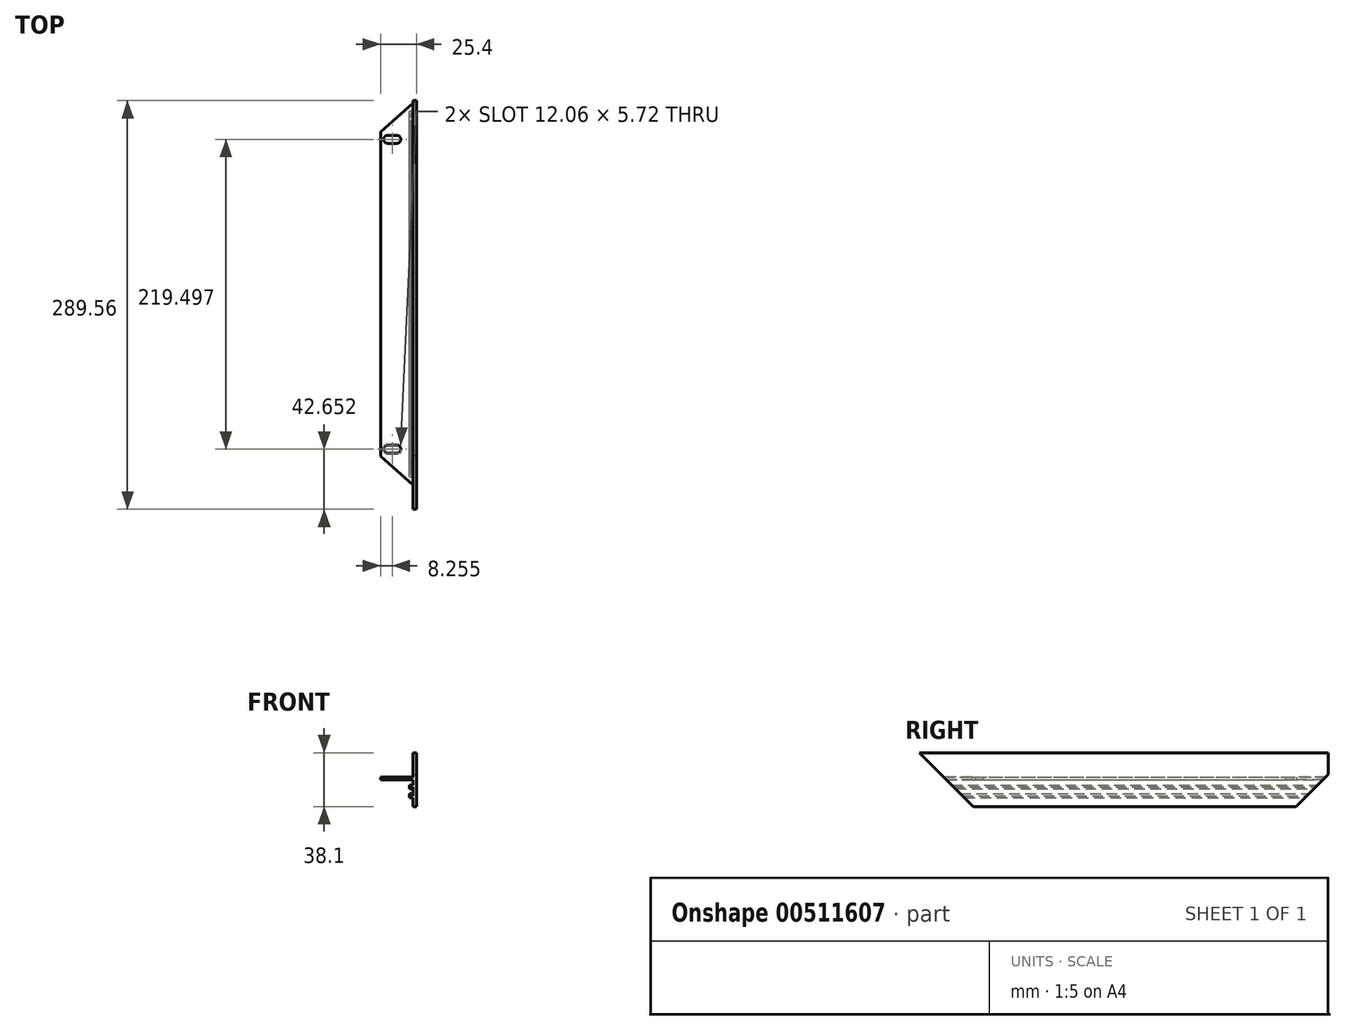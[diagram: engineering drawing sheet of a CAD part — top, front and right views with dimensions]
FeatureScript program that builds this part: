
annotation { "Feature Type Name" : "Feature", "Feature Type Description" : "" }
export const myFeature = defineFeature(function(context is Context, id is Id, definition is map)
    precondition{}
    {
        {
            var Q0;
            Q0=qCreatedBy(makeId("Front.planeOp"),FACE);
            var sketch = newSketch(context, id + "F0", { "sketchPlane" : qUnion([Q0])});
            skLineSegment(sketch, "E0", {"start": v(0, 0) * mm, "end": v(0, 38.1) * mm});
            skLineSegment(sketch, "E1", {"start": v(0, 38.1) * mm, "end": v(-2.54, 38.1) * mm});
            skLineSegment(sketch, "E2", {"start": v(-2.54, 38.1) * mm, "end": v(-2.54, 20.96) * mm});
            skLineSegment(sketch, "E3", {"start": v(-2.54, 20.96) * mm, "end": v(-25.4, 20.95) * mm});
            skLineSegment(sketch, "E4", {"start": v(-25.4, 20.95) * mm, "end": v(-25.4, 19.05) * mm});
            skLineSegment(sketch, "E5", {"start": v(-25.4, 19.05) * mm, "end": v(-2.54, 19.05) * mm});
            skLineSegment(sketch, "E6", {"start": v(-2.54, 6.35) * mm, "end": v(-2.54, 0) * mm});
            skLineSegment(sketch, "E7", {"start": v(-2.54, 0) * mm, "end": v(0, 0) * mm});
            skLineSegment(sketch, "E8", {"start": v(-5.08, 15.24) * mm, "end": v(-5.08, 12.45) * mm});
            skLineSegment(sketch, "E9", {"start": v(-5.08, 6.35) * mm, "end": v(-2.54, 6.35) * mm});
            skLineSegment(sketch, "E10.bottom", {"start": v(-3.8, 7.62) * mm, "end": v(-2.54, 7.62) * mm});
            skLineSegment(sketch, "E10.top", {"start": v(-3.81, 13.97) * mm, "end": v(-2.54, 13.97) * mm});
            skLineSegment(sketch, "E10.left", {"start": v(-3.8, 7.62) * mm, "end": v(-3.8, 9.14) * mm});
            skLineSegment(sketch, "E10.right", {"start": v(-2.54, 7.62) * mm, "end": v(-2.54, 13.97) * mm});
            skLineSegment(sketch, "E11", {"start": v(-5.08, 15.24) * mm, "end": v(-2.54, 15.24) * mm});
            skLineSegment(sketch, "E12", {"start": v(-2.54, 15.24) * mm, "end": v(-2.54, 19.05) * mm});
            skLineSegment(sketch, "E13", {"start": v(-5.08, 12.45) * mm, "end": v(-3.81, 12.45) * mm});
            skLineSegment(sketch, "E14", {"start": v(-3.8, 9.14) * mm, "end": v(-5.08, 9.14) * mm});
            skLineSegment(sketch, "E15.trimOffspring", {"start": v(-5.08, 9.14) * mm, "end": v(-5.08, 6.35) * mm});
            skLineSegment(sketch, "E16.trimOffspring", {"start": v(-3.81, 12.45) * mm, "end": v(-3.81, 13.97) * mm});
            skSolve(sketch);
        }
        {
            var Q0;
            Q0=makeQuery(id+"F0.imprint","IMPRINT",FACE,{"disambiguationData":[TD([[makeQuery(id+"F0.imprint","IMPRINT",EDGE,{"derivedFrom":sQuery(id+"F0.wireOp",EDGE,"E0")}),1.0]])]});
            extrude(context, id + "F1", {"entities" : qUnion([Q0]), "depth" : 304.8 * mm});
        }
        {
            var Q0;
            Q0=makeQuery(id+"F1.opExtrude","SWEPT_FACE",FACE,{"disambiguationData":[OSD([sQuery(id+"F0.wireOp",EDGE,"E0")])]});
            var sketch = newSketch(context, id + "F2", { "sketchPlane" : qUnion([Q0])});
            skLineSegment(sketch, "E17", {"start": v(-304.8, 38.1) * mm, "end": v(-266.7, 0) * mm});
            skLineSegment(sketch, "E18", {"start": v(-266.7, 0) * mm, "end": v(-304.8, 0) * mm});
            skLineSegment(sketch, "E19", {"start": v(-304.8, 0) * mm, "end": v(-304.8, 38.1) * mm});
            skLineSegment(sketch, "E20", {"start": v(0, 38.1) * mm, "end": v(0, 0) * mm});
            skLineSegment(sketch, "E21", {"start": v(0, 0) * mm, "end": v(-38.1, 0) * mm});
            skLineSegment(sketch, "E22", {"start": v(-38.1, 0) * mm, "end": v(0, 38.1) * mm});
            skSolve(sketch);
        }
        {
            var Q0;
            Q0=qSketchRegion(id+"F2",true);
            extrude(context, id + "F3", {"entities" : qUnion([Q0]), "operationType" : NewBodyOperationType.REMOVE, "oppositeDirection" : true, "depth" : 25.4 * mm});
        }
        {
            var Q0;
            Q0=makeQuery(id+"F1.opExtrude","SWEPT_FACE",FACE,{"disambiguationData":[OSD([sQuery(id+"F0.wireOp",EDGE,"E3")])]});
            var sketch = newSketch(context, id + "F4", { "sketchPlane" : qUnion([Q0])});
            skLineSegment(sketch, "E23", {"start": v(-2.54, -17.15) * mm, "end": v(-25.4, -37.47) * mm});
            skLineSegment(sketch, "E24", {"start": v(-25.4, -37.47) * mm, "end": v(-25.4, -17.15) * mm});
            skLineSegment(sketch, "E25", {"start": v(-25.4, -17.15) * mm, "end": v(-2.54, -17.15) * mm});
            skLineSegment(sketch, "E26", {"start": v(-2.54, -287.66) * mm, "end": v(-25.4, -287.66) * mm});
            skLineSegment(sketch, "E27", {"start": v(-25.4, -287.66) * mm, "end": v(-25.4, -267.34) * mm});
            skLineSegment(sketch, "E28", {"start": v(-25.4, -267.34) * mm, "end": v(-2.54, -287.66) * mm});
            skSolve(sketch);
        }
        {
            var Q0;
            Q0=qSketchRegion(id+"F4",true);
            extrude(context, id + "F5", {"entities" : qUnion([Q0]), "operationType" : NewBodyOperationType.REMOVE, "oppositeDirection" : true, "depth" : 25.4 * mm});
        }
        {
            var Q0;
            Q0=makeQuery(id+"F1.opExtrude","SWEPT_FACE",FACE,{"disambiguationData":[OSD([sQuery(id+"F0.wireOp",EDGE,"E3")])]});
            var sketch = newSketch(context, id + "F6", { "sketchPlane" : qUnion([Q0])});
            skLineSegment(sketch, "E29", {"start": v(-25.4, -37.47) * mm, "end": v(-2.54, -37.47) * mm, "construction": true});
            skLineSegment(sketch, "E30", {"start": v(-2.54, -37.47) * mm, "end": v(-13.97, -27.3) * mm, "construction": true});
            skLineSegment(sketch, "E31", {"start": v(-13.97, -27.3) * mm, "end": v(-25.4, -37.47) * mm, "construction": true});
            skLineSegment(sketch, "E32", {"start": v(-20.32, -39.8) * mm, "end": v(-13.97, -39.8) * mm});
            skLineSegment(sketch, "E33", {"start": v(-20.32, -45.5) * mm, "end": v(-13.97, -45.5) * mm});
            skArc(sketch, "E34", {"start": v(-20.32, -39.8) * mm, "mid": v(-23.18, -42.65) * mm, "end": v(-20.32, -45.5) * mm});
            skArc(sketch, "E35", {"start": v(-13.97, -39.8) * mm, "mid": v(-11.11, -42.65) * mm, "end": v(-13.97, -45.5) * mm});
            skLineSegment(sketch, "E36", {"start": v(-2.54, -152.4) * mm, "end": v(-25.4, -152.4) * mm, "construction": true});
            skArc(sketch, "E37.MirrorCS", {"start": v(-13.97, -265) * mm, "mid": v(-11.11, -262.15) * mm, "end": v(-13.97, -259.3) * mm});
            skArc(sketch, "E38.MirrorCS", {"start": v(-20.32, -265) * mm, "mid": v(-23.18, -262.15) * mm, "end": v(-20.32, -259.3) * mm});
            skLineSegment(sketch, "E39.MirrorCS", {"start": v(-20.32, -259.3) * mm, "end": v(-13.97, -259.3) * mm});
            skLineSegment(sketch, "E40.MirrorCS", {"start": v(-25.4, -267.34) * mm, "end": v(-2.54, -267.34) * mm, "construction": true});
            skLineSegment(sketch, "E41.MirrorCS", {"start": v(-2.54, -267.33) * mm, "end": v(-13.97, -277.5) * mm, "construction": true});
            skLineSegment(sketch, "E42.MirrorCS", {"start": v(-13.97, -277.5) * mm, "end": v(-25.4, -267.34) * mm, "construction": true});
            skLineSegment(sketch, "E43.MirrorCS", {"start": v(-20.32, -265) * mm, "end": v(-13.97, -265) * mm});
            skSolve(sketch);
        }
        {
            var Q0;
            Q0=qSketchRegion(id+"F6",true);
            extrude(context, id + "F7", {"entities" : qUnion([Q0]), "operationType" : NewBodyOperationType.REMOVE, "oppositeDirection" : true, "depth" : 25.4 * mm});
        }
        {
            var Q0;
            Q0=makeQuery(id+"F1.opExtrude","SWEPT_FACE",FACE,{"disambiguationData":[OSD([sQuery(id+"F0.wireOp",EDGE,"E0")])]});
            var sketch = newSketch(context, id + "F8", { "sketchPlane" : qUnion([Q0])});
            skLineSegment(sketch, "E44", {"start": v(0, 38.1) * mm, "end": v(-15.24, 38.1) * mm});
            skLineSegment(sketch, "E45", {"start": v(-15.24, 38.1) * mm, "end": v(-15.24, 22.86) * mm});
            skLineSegment(sketch, "E46", {"start": v(-15.24, 22.86) * mm, "end": v(0, 38.1) * mm});
            skSolve(sketch);
        }
        {
            var Q0;
            Q0=qSketchRegion(id+"F8",true);
            extrude(context, id + "F9", {"entities" : qUnion([Q0]), "operationType" : NewBodyOperationType.REMOVE, "oppositeDirection" : true, "depth" : 25.4 * mm});
        }
    });
